# Revit family: Faucet-Bath_Filler-KOHLER-Tempered-K-T22025_1
name_source: partatom
category: Plumbing Fixtures
revit_build: Autodesk Revit 2017 (Build: 20160225_1515(x64)
units: mm (PartAtom-declared; Revit-internal decimal feet)

## family parameters
Cut with Voids When Loaded = No
Host = Face
OmniClass Number = 23.31.11.00
OmniClass Title = Faucets
Part Type = Normal
Room Calculation Point = No
Round Connector Dimension = Use Diameter
Shared = No

## types (4) — shared parameters
ADA Compliant = No
Assembly Code = D2010
CW Connection = Yes
Cold Water Inlet = Cold Water Inlet
Date Modified = 01/30/2020
Default Elevation = 0"
Description = Floor-mount bath filler trim with handshower
Drain Included = No
Flow Rate = 9 GPM
HW Connection = Yes
Handle Clearance = 3 5/16"
Height = 37 1/16"
Hot Water Inlet = Hot Water Inlet
Length = 10 3/16"
Manufacturer = KOHLER Co.
MasterFormat 1995 = 15410
MasterFormat 2004 = 22.41.39
Material = Premium Metal Construction
Pressure = 45.00 psi
Product Documentation Link = https://www.us.kohler.com
Product Name = Tempered
Product Page URL = http://www.us.kohler.com
Spout Reach = 10 3/16"
URL = https://www.us.kohler.com
Vent Connection = No
Waste Connection = No
Waste Water Outlet = Waste Water Outlet
WaterSense Certified = Yes
Width = 4 7/8"

## per-type parameters (varying)
| type | Finish | Model | Type |
| CP-Polished Chrome | Kohler-Metal-CP-Polished_Chrome | K-T22025-4-CP | 1 |
| SN-Vibrant Polished Nickel | Kohler-Metal-SN-Vibrant_Polished_Nickel | K-T22025-4-SN | 2 |
| BN-Vibrant Brushed Nickel | Kohler-Metal-BN-Vibrant_Brushed_Nickel | K-T22025-4-BN | 3 |
| BL-Matte Black | Kohler-Metal-BL-Matte_Black | K-T22025-4-BL | 4 |

## geometry (parser evidence)
native form markers: Sweep x6
no freeform markers — native parametric forms only
